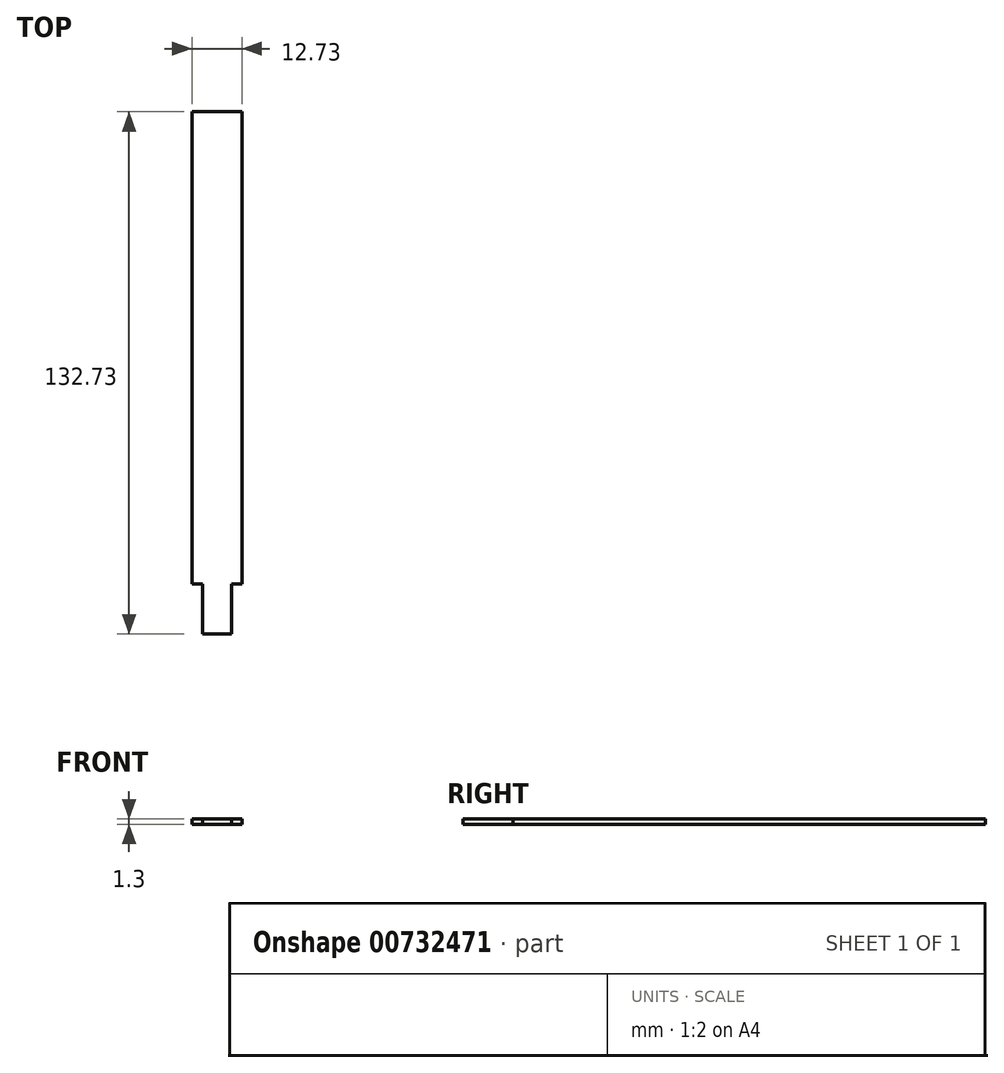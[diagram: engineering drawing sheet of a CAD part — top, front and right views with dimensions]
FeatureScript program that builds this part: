
annotation { "Feature Type Name" : "Feature", "Feature Type Description" : "" }
export const myFeature = defineFeature(function(context is Context, id is Id, definition is map)
    precondition{}
    {
        {
            var Q0;
            Q0=qCreatedBy(makeId("Top.planeOp"),FACE);
            var sketch = newSketch(context, id + "F0", { "sketchPlane" : qUnion([Q0])});
            skLineSegment(sketch, "E0.bottom", {"start": v(-24.87, 59.91) * mm, "end": v(-12.14, 59.91) * mm});
            skLineSegment(sketch, "E0.top", {"start": v(-24.87, -60.09) * mm, "end": v(-12.14, -60.09) * mm});
            skLineSegment(sketch, "E0.left", {"start": v(-24.87, 59.91) * mm, "end": v(-24.87, -60.09) * mm});
            skLineSegment(sketch, "E0.right", {"start": v(-12.14, 59.91) * mm, "end": v(-12.14, -60.09) * mm});
            skSolve(sketch);
        }
        {
            var Q0;
            Q0=qSketchRegion(id+"F0",true);
            extrude(context, id + "F1", {"entities" : qUnion([Q0]), "depth" : 1.3 * mm, "offsetDistance" : 25.4 * mm});
        }
        {
            var Q0;
            Q0=qCreatedBy(makeId("Top.planeOp"),FACE);
            var sketch = newSketch(context, id + "F2", { "sketchPlane" : qUnion([Q0])});
            skLineSegment(sketch, "E1.bottom", {"start": v(-22.15, -59.82) * mm, "end": v(-14.85, -59.82) * mm});
            skLineSegment(sketch, "E1.top", {"start": v(-22.15, -72.82) * mm, "end": v(-14.85, -72.82) * mm});
            skLineSegment(sketch, "E1.left", {"start": v(-22.15, -59.82) * mm, "end": v(-22.15, -72.82) * mm});
            skLineSegment(sketch, "E1.right", {"start": v(-14.85, -59.82) * mm, "end": v(-14.85, -72.82) * mm});
            skSolve(sketch);
        }
        {
            var Q0;
            Q0 = qSketchRegion(id + "F2", true);
            extrude(context, id + "F3", {"entities" : qUnion([Q0]), "operationType" : NewBodyOperationType.ADD, "depth" : 1.3 * mm, "offsetDistance" : 25.4 * mm});
        }
    });
